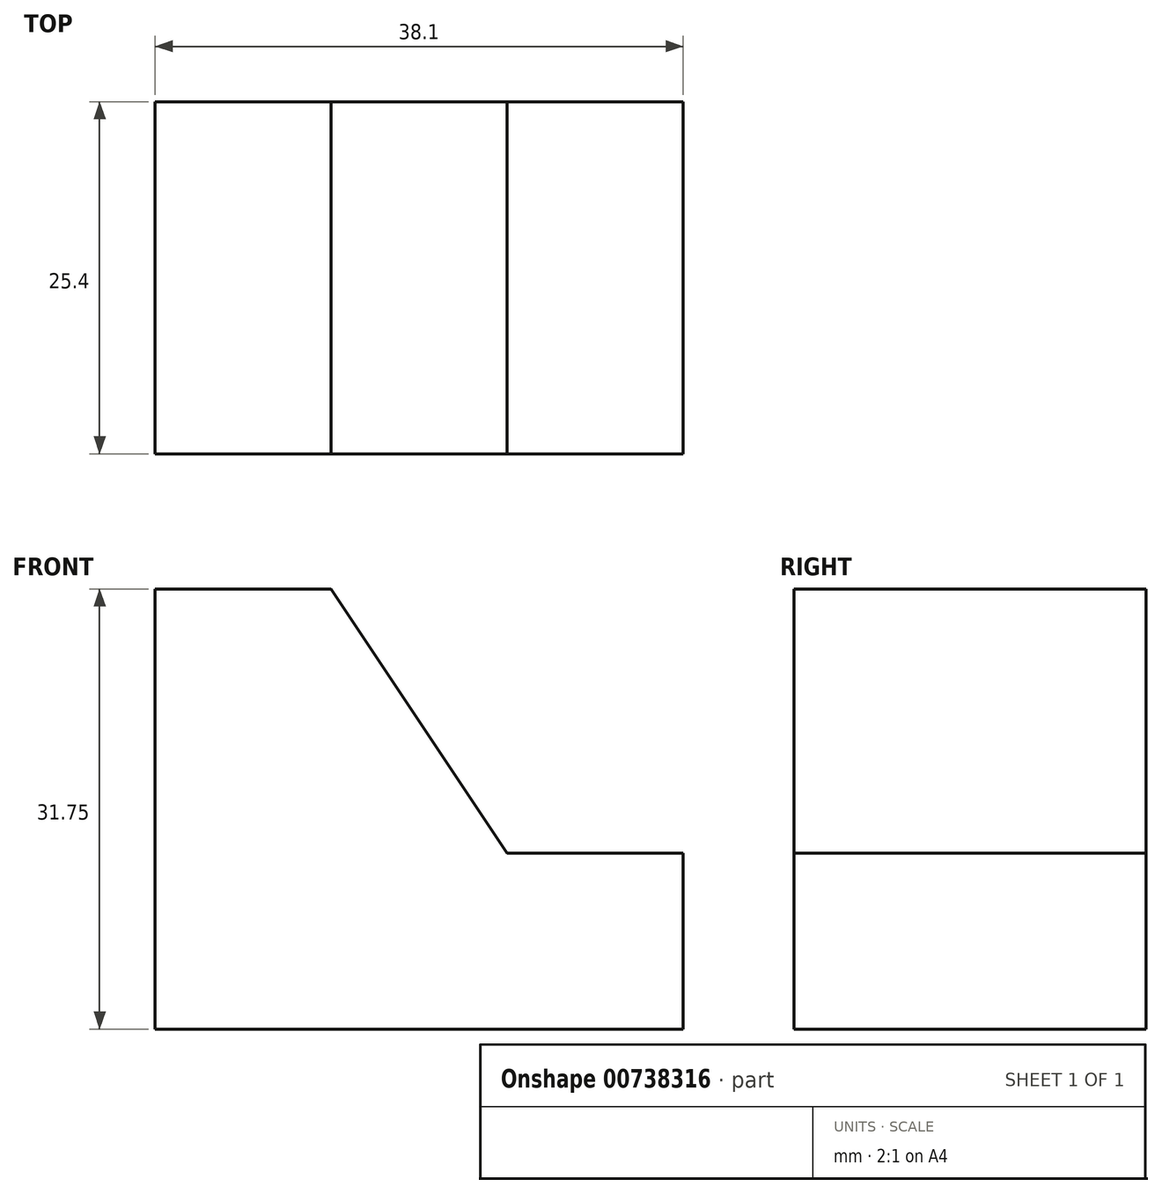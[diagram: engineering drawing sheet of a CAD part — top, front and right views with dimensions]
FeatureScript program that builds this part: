
annotation { "Feature Type Name" : "Feature", "Feature Type Description" : "" }
export const myFeature = defineFeature(function(context is Context, id is Id, definition is map)
    precondition{}
    {
        {
            var Q0;
            Q0=qCreatedBy(makeId("Front.planeOp"),FACE);
            var sketch = newSketch(context, id + "F0", { "sketchPlane" : qUnion([Q0])});
            skLineSegment(sketch, "E0", {"start": v(0, 0) * mm, "end": v(0, 31.75) * mm});
            skLineSegment(sketch, "E1", {"start": v(0, 31.75) * mm, "end": v(12.7, 31.75) * mm});
            skLineSegment(sketch, "E2", {"start": v(12.7, 31.75) * mm, "end": v(25.4, 12.7) * mm});
            skLineSegment(sketch, "E3", {"start": v(25.4, 12.7) * mm, "end": v(38.1, 12.7) * mm});
            skLineSegment(sketch, "E4", {"start": v(38.1, 12.7) * mm, "end": v(38.1, 0) * mm});
            skLineSegment(sketch, "E5", {"start": v(38.1, 0) * mm, "end": v(0, 0) * mm});
            skSolve(sketch);
        }
        {
            var Q0;
            Q0=makeQuery(id+"F0.imprint","IMPRINT",FACE,{"disambiguationData":[TD([[makeQuery(id+"F0.imprint","IMPRINT",EDGE,{"derivedFrom":sQuery(id+"F0.wireOp",EDGE,"E0")}),-1.0]])]});
            extrude(context, id + "F1", {"entities" : qUnion([Q0]), "depth" : 25.4 * mm, "offsetDistance" : 25.4 * mm});
        }
    });
